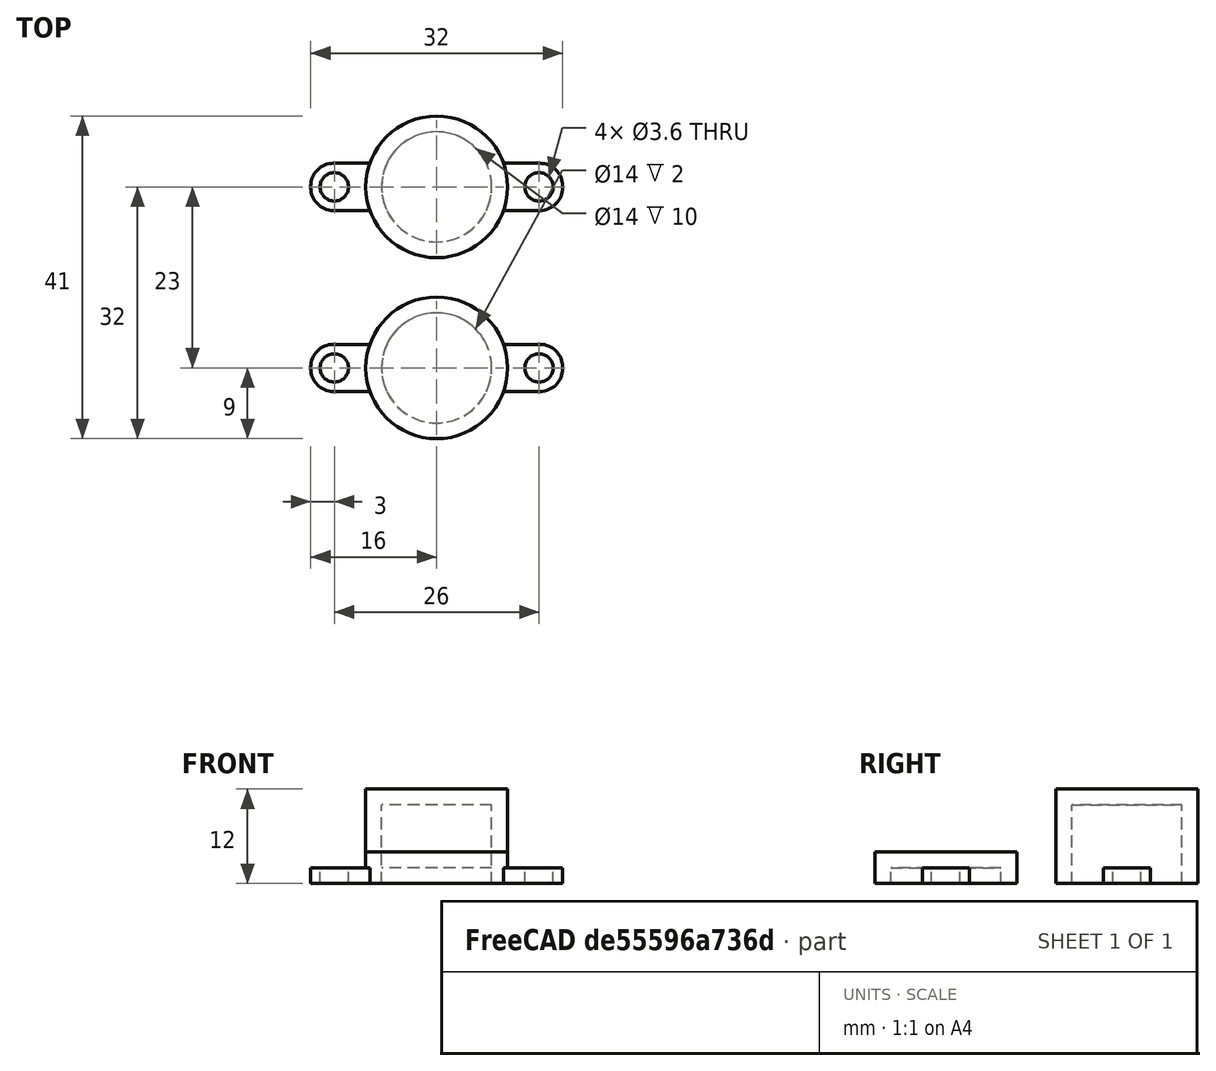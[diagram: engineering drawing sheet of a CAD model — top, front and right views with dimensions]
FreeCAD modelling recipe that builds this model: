
FCSTD DOCUMENT  (FreeCAD 0.19R24291 (Git))
Label: ref_cover
License: All rights reserved
LicenseURL: http://en.wikipedia.org/wiki/All_rights_reserved
objects: Part::Cylinder×8, Part::MultiFuse×4, Part::Box×2, Part::Fillet×2, Part::Cut×2
note: 18 computed .brp shape members not serialized (recipe doc carries the construction recipe); baked Part::Feature solids carry a one-line shape summary decoded from their .brp

FEATURE [Part::Cylinder] Cylinder
  Angle = 360
  AttacherType = Attacher::AttachEngine3D
  Height = 10
  Radius = 7
FEATURE [Part::Cylinder] Cylinder001
  Angle = 360
  AttacherType = Attacher::AttachEngine3D
  Height = 12
  Radius = 9
FEATURE [Part::Box] Box  label="Cube"
  AttacherType = Attacher::AttachEngine3D
  Height = 2
  Length = 32
  Placement = pos=(-16,-3,0) rot=(0,0,1;0rad)
  Width = 6
FEATURE [Part::Cylinder] Cylinder002
  Angle = 360
  AttacherType = Attacher::AttachEngine3D
  Height = 3
  Placement = pos=(-13,0,0) rot=(0,0,1;0rad)
  Radius = 1.8
FEATURE [Part::Cylinder] Cylinder003
  Angle = 360
  AttacherType = Attacher::AttachEngine3D
  Height = 3
  Placement = pos=(13,0,0) rot=(0,0,1;0rad)
  Radius = 1.8
FEATURE [Part::Fillet] Fillet
  Base = -> Box
  Edges = 4 edges r=2.9: [Edge1,Edge3,Edge5,Edge7]
FEATURE [Part::MultiFuse] Fusion
  Shapes = -> [Cylinder001,Fillet]
FEATURE [Part::MultiFuse] Fusion001
  Shapes = -> [Cylinder003,Cylinder002,Cylinder]
FEATURE [Part::Cut] Cut
  Base = -> Fusion
  Tool = -> Fusion001
FEATURE [Part::Cylinder] Cylinder004
  Angle = 360
  AttacherType = Attacher::AttachEngine3D
  Height = 2
  Radius = 7
FEATURE [Part::Box] Box001  label="Cube001"
  AttacherType = Attacher::AttachEngine3D
  Height = 2
  Length = 32
  Placement = pos=(-16,-3,0) rot=(0,0,1;0rad)
  Width = 6
FEATURE [Part::Cylinder] Cylinder005
  Angle = 360
  AttacherType = Attacher::AttachEngine3D
  Height = 3
  Placement = pos=(13,0,0) rot=(0,0,1;0rad)
  Radius = 1.8
FEATURE [Part::Cylinder] Cylinder006
  Angle = 360
  AttacherType = Attacher::AttachEngine3D
  Height = 3
  Placement = pos=(-13,0,0) rot=(0,0,1;0rad)
  Radius = 1.8
FEATURE [Part::MultiFuse] Fusion002
  Shapes = -> [Cylinder005,Cylinder006,Cylinder004]
FEATURE [Part::Fillet] Fillet001
  Base = -> Box001
  Edges = 4 edges r=2.9: [Edge1,Edge3,Edge5,Edge7]
FEATURE [Part::Cylinder] Cylinder007
  Angle = 360
  AttacherType = Attacher::AttachEngine3D
  Height = 4
  Radius = 9
FEATURE [Part::MultiFuse] Fusion003
  Shapes = -> [Cylinder007,Fillet001]
FEATURE [Part::Cut] Cut001
  Base = -> Fusion003
  Placement = pos=(0,-23,0) rot=(0,0,1;0rad)
  Tool = -> Fusion002
